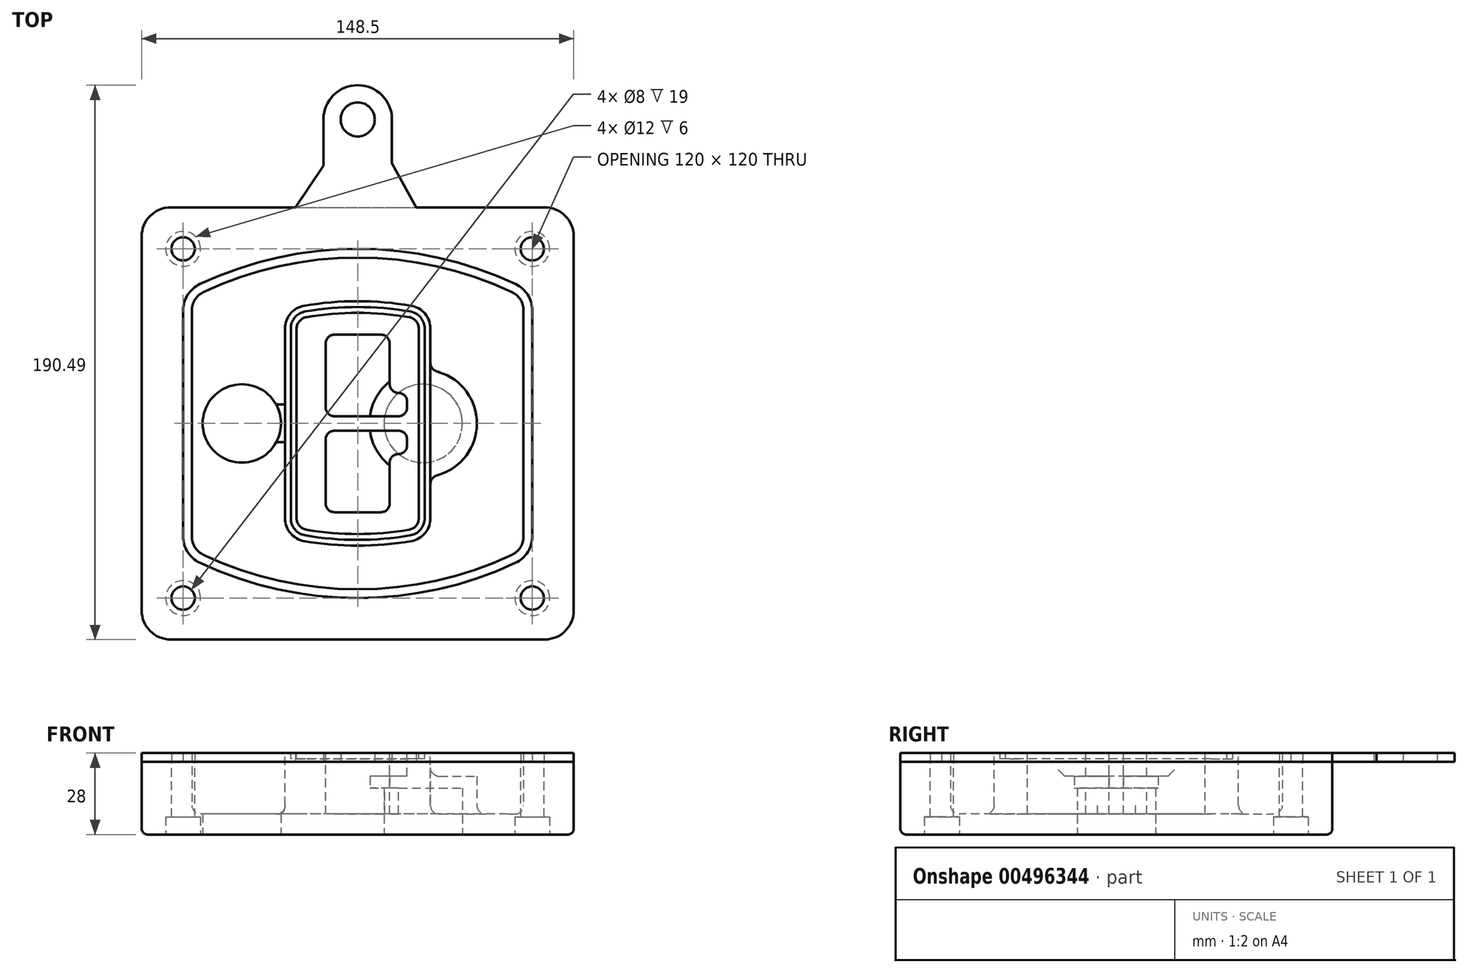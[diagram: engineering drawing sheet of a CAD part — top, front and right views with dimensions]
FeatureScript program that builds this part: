
annotation { "Feature Type Name" : "Feature", "Feature Type Description" : "" }
export const myFeature = defineFeature(function(context is Context, id is Id, definition is map)
    precondition{}
    {
        {
            var Q0;
            Q0=qCreatedBy(makeId("Top.planeOp"),FACE);
            var sketch = newSketch(context, id + "F0", { "sketchPlane" : qUnion([Q0])});
            skPoint(sketch, "E0.rect.middle", {"position": v(0, 0) * mm});
            skLineSegment(sketch, "E1.bottom", {"start": v(-64.25, -74.25) * mm, "end": v(64.25, -74.25) * mm});
            skLineSegment(sketch, "E1.top", {"start": v(-64.25, 74.25) * mm, "end": v(64.25, 74.25) * mm});
            skLineSegment(sketch, "E1.left", {"start": v(-74.25, -64.25) * mm, "end": v(-74.25, 64.25) * mm});
            skLineSegment(sketch, "E1.right", {"start": v(74.25, -64.25) * mm, "end": v(74.25, 64.25) * mm});
            skLineSegment(sketch, "E2", {"start": v(-74.25, 74.25) * mm, "end": v(74.25, -74.25) * mm, "construction": true});
            skLineSegment(sketch, "E3", {"start": v(74.25, 74.25) * mm, "end": v(-74.25, -74.25) * mm, "construction": true});
            skCircle(sketch, "E4", {"center": v(-60, 60) * mm, "radius": 4 * mm});
            skCircle(sketch, "E5", {"center": v(60, 60) * mm, "radius": 4 * mm});
            skCircle(sketch, "E6", {"center": v(60, -60) * mm, "radius": 4 * mm});
            skCircle(sketch, "E7", {"center": v(-60, -60) * mm, "radius": 4 * mm});
            skLineSegment(sketch, "E8", {"start": v(-60, 60) * mm, "end": v(60, 60) * mm, "construction": true});
            skLineSegment(sketch, "E9", {"start": v(60, 60) * mm, "end": v(60, -60) * mm, "construction": true});
            skLineSegment(sketch, "E10", {"start": v(60, -60) * mm, "end": v(-60, -60) * mm, "construction": true});
            skLineSegment(sketch, "E11", {"start": v(-60, -60) * mm, "end": v(-60, 60) * mm, "construction": true});
            skLineSegment(sketch, "E12", {"start": v(-60, 38.83) * mm, "end": v(-60, -38.83) * mm});
            skLineSegment(sketch, "E13", {"start": v(60, 38.83) * mm, "end": v(60, -38.83) * mm});
            skArc(sketch, "E14", {"start": v(54.26, 47.88) * mm, "mid": v(0, 60) * mm, "end": v(-54.26, 47.88) * mm});
            skArc(sketch, "E15", {"start": v(-54.26, -47.88) * mm, "mid": v(0, -60) * mm, "end": v(54.26, -47.88) * mm});
            skLineSegment(sketch, "E16", {"start": v(-60, 0) * mm, "end": v(60, 0) * mm, "construction": true});
            skPoint(sketch, "E17.visualSharp", {"position": v(-60, -45) * mm});
            skArc(sketch, "E17.filletArc", {"start": v(-60, -38.83) * mm, "mid": v(-58.44, -44.2) * mm, "end": v(-54.26, -47.88) * mm});
            skPoint(sketch, "E18.visualSharp", {"position": v(-60, 45) * mm});
            skArc(sketch, "E18.filletArc", {"start": v(-54.26, 47.88) * mm, "mid": v(-58.44, 44.2) * mm, "end": v(-60, 38.83) * mm});
            skPoint(sketch, "E19.visualSharp", {"position": v(60, 45) * mm});
            skArc(sketch, "E19.filletArc", {"start": v(60, 38.83) * mm, "mid": v(58.44, 44.2) * mm, "end": v(54.26, 47.88) * mm});
            skPoint(sketch, "E20.visualSharp", {"position": v(60, -45) * mm});
            skArc(sketch, "E20.filletArc", {"start": v(54.26, -47.88) * mm, "mid": v(58.44, -44.2) * mm, "end": v(60, -38.83) * mm});
            skPoint(sketch, "E21.visualSharp", {"position": v(-74.25, 74.25) * mm});
            skArc(sketch, "E21.filletArc", {"start": v(-64.25, 74.25) * mm, "mid": v(-71.32, 71.32) * mm, "end": v(-74.25, 64.25) * mm});
            skPoint(sketch, "E22.visualSharp", {"position": v(74.25, 74.25) * mm});
            skArc(sketch, "E22.filletArc", {"start": v(74.25, 64.25) * mm, "mid": v(71.32, 71.32) * mm, "end": v(64.25, 74.25) * mm});
            skPoint(sketch, "E23.visualSharp", {"position": v(74.25, -74.25) * mm});
            skArc(sketch, "E23.filletArc", {"start": v(64.25, -74.25) * mm, "mid": v(71.32, -71.32) * mm, "end": v(74.25, -64.25) * mm});
            skPoint(sketch, "E24.visualSharp", {"position": v(-74.25, -74.25) * mm});
            skArc(sketch, "E24.filletArc", {"start": v(-74.25, -64.25) * mm, "mid": v(-71.32, -71.32) * mm, "end": v(-64.25, -74.25) * mm});
            skArc(sketch, "E25.0", {"start": v(57, 38.83) * mm, "mid": v(55.9, 42.58) * mm, "end": v(52.98, 45.17) * mm});
            skLineSegment(sketch, "E25.1", {"start": v(57, 38.83) * mm, "end": v(57, -38.83) * mm});
            skArc(sketch, "E25.2", {"start": v(52.98, -45.17) * mm, "mid": v(55.9, -42.58) * mm, "end": v(57, -38.83) * mm});
            skArc(sketch, "E25.3", {"start": v(-52.98, -45.17) * mm, "mid": v(0, -57) * mm, "end": v(52.98, -45.17) * mm});
            skArc(sketch, "E25.4", {"start": v(-57, -38.83) * mm, "mid": v(-55.9, -42.58) * mm, "end": v(-52.98, -45.17) * mm});
            skArc(sketch, "E25.5", {"start": v(52.98, 45.17) * mm, "mid": v(0, 57) * mm, "end": v(-52.98, 45.17) * mm});
            skLineSegment(sketch, "E25.6", {"start": v(-57, 38.83) * mm, "end": v(-57, -38.83) * mm});
            skArc(sketch, "E25.7", {"start": v(-52.98, 45.17) * mm, "mid": v(-55.9, 42.58) * mm, "end": v(-57, 38.83) * mm});
            skArc(sketch, "E26.0", {"start": v(-55.96, 51.5) * mm, "mid": v(-61.82, 46.33) * mm, "end": v(-64, 38.83) * mm});
            skArc(sketch, "E26.1", {"start": v(55.96, 51.5) * mm, "mid": v(0, 64) * mm, "end": v(-55.96, 51.5) * mm});
            skArc(sketch, "E26.2", {"start": v(64, 38.83) * mm, "mid": v(61.82, 46.33) * mm, "end": v(55.96, 51.5) * mm});
            skLineSegment(sketch, "E26.3", {"start": v(64, 38.83) * mm, "end": v(64, -38.83) * mm});
            skArc(sketch, "E26.4", {"start": v(55.96, -51.5) * mm, "mid": v(61.82, -46.33) * mm, "end": v(64, -38.83) * mm});
            skLineSegment(sketch, "E26.5", {"start": v(-64, 38.83) * mm, "end": v(-64, -38.83) * mm});
            skArc(sketch, "E26.6", {"start": v(-55.96, -51.5) * mm, "mid": v(0, -64) * mm, "end": v(55.96, -51.5) * mm});
            skArc(sketch, "E26.7", {"start": v(-64, -38.83) * mm, "mid": v(-61.82, -46.33) * mm, "end": v(-55.96, -51.5) * mm});
            skSolve(sketch);
        }
        {
            var Q0;
            Q0=makeQuery(id+"F0.imprint","IMPRINT",FACE,{"disambiguationData":[TD([[makeQuery(id+"F0.imprint","IMPRINT",EDGE,{"derivedFrom":sQuery(id+"F0.wireOp",EDGE,"E1.bottom")}),1.0]])]});
            var Q1;
            Q1=makeQuery(id+"F0.imprint","IMPRINT",FACE,{"disambiguationData":[TD([[makeQuery(id+"F0.imprint","IMPRINT",EDGE,{"derivedFrom":sQuery(id+"F0.wireOp",EDGE,"E12")}),1.0]])]});
            var Q2;
            Q2=makeQuery(id+"F0.imprint","IMPRINT",FACE,{"disambiguationData":[TD([[makeQuery(id+"F0.imprint","IMPRINT",EDGE,{"derivedFrom":sQuery(id+"F0.wireOp",EDGE,"E25.0")}),1.0]])]});
            var Q3;
            Q3=makeQuery(id+"F0.imprint","IMPRINT",FACE,{"disambiguationData":[TD([[makeQuery(id+"F0.imprint","IMPRINT",EDGE,{"derivedFrom":sQuery(id+"F0.wireOp",EDGE,"E12")}),-1.0]])]});
            extrude(context, id + "F1", {"entities" : qUnion([Q0, Q1, Q2, Q3]), "oppositeDirection" : true, "depth" : 25 * mm});
        }
        {
            var Q0;
            Q0=makeQuery(id+"F0.imprint","IMPRINT",FACE,{"disambiguationData":[TD([[makeQuery(id+"F0.imprint","IMPRINT",EDGE,{"derivedFrom":sQuery(id+"F0.wireOp",EDGE,"E12")}),1.0]])]});
            extrude(context, id + "F2", {"entities" : qUnion([Q0]), "operationType" : NewBodyOperationType.ADD, "depth" : 3 * mm});
        }
        {
            var Q0;
            Q0=makeQuery(id+"F0.imprint","IMPRINT",FACE,{"disambiguationData":[TD([[makeQuery(id+"F0.imprint","IMPRINT",EDGE,{"derivedFrom":sQuery(id+"F0.wireOp",EDGE,"E25.0")}),1.0]])]});
            extrude(context, id + "F3", {"entities" : qUnion([Q0]), "operationType" : NewBodyOperationType.REMOVE, "oppositeDirection" : true, "depth" : 18 * mm});
        }
        {
            var Q0;
            Q0=makeQuery(id+"F2.opExtrude","CAP_FACE",FACE,{"disambiguationData":[OSD([sQuery(id+"F0.wireOp",EDGE,"E12"),sQuery(id+"F0.wireOp",EDGE,"E13"),sQuery(id+"F0.wireOp",EDGE,"E14"),sQuery(id+"F0.wireOp",EDGE,"E15"),sQuery(id+"F0.wireOp",EDGE,"E17.filletArc"),sQuery(id+"F0.wireOp",EDGE,"E18.filletArc"),sQuery(id+"F0.wireOp",EDGE,"E19.filletArc"),sQuery(id+"F0.wireOp",EDGE,"E20.filletArc"),sQuery(id+"F0.wireOp",EDGE,"E25.0"),sQuery(id+"F0.wireOp",EDGE,"E25.1"),sQuery(id+"F0.wireOp",EDGE,"E25.2"),sQuery(id+"F0.wireOp",EDGE,"E25.3"),sQuery(id+"F0.wireOp",EDGE,"E25.4"),sQuery(id+"F0.wireOp",EDGE,"E25.5"),sQuery(id+"F0.wireOp",EDGE,"E25.6"),sQuery(id+"F0.wireOp",EDGE,"E25.7")])],"isStart":false});
            var sketch = newSketch(context, id + "F4", { "sketchPlane" : qUnion([Q0])});
            skArc(sketch, "E27.0", {"start": v(-18.34, -40.45) * mm, "mid": v(0, -42) * mm, "end": v(18.34, -40.45) * mm});
            skArc(sketch, "E28.0", {"start": v(18.34, 40.45) * mm, "mid": v(0, 42) * mm, "end": v(-18.34, 40.45) * mm});
            skLineSegment(sketch, "E29", {"start": v(-25, 32.57) * mm, "end": v(-25, -32.57) * mm});
            skLineSegment(sketch, "E30", {"start": v(25, 32.57) * mm, "end": v(25, -32.57) * mm});
            skLineSegment(sketch, "E31", {"start": v(-25, 39.1) * mm, "end": v(25, 39.1) * mm, "construction": true});
            skLineSegment(sketch, "E32", {"start": v(-25, -39.1) * mm, "end": v(25, -39.1) * mm, "construction": true});
            skPoint(sketch, "E33.visualSharp", {"position": v(-25, 39.1) * mm});
            skArc(sketch, "E33.filletArc", {"start": v(-18.34, 40.45) * mm, "mid": v(-23.11, 37.73) * mm, "end": v(-25, 32.57) * mm});
            skPoint(sketch, "E34.visualSharp", {"position": v(25, 39.1) * mm});
            skArc(sketch, "E34.filletArc", {"start": v(25, 32.57) * mm, "mid": v(23.11, 37.73) * mm, "end": v(18.34, 40.45) * mm});
            skPoint(sketch, "E35.visualSharp", {"position": v(25, -39.1) * mm});
            skArc(sketch, "E35.filletArc", {"start": v(18.34, -40.45) * mm, "mid": v(23.11, -37.73) * mm, "end": v(25, -32.57) * mm});
            skPoint(sketch, "E36.visualSharp", {"position": v(-25, -39.1) * mm});
            skArc(sketch, "E36.filletArc", {"start": v(-25, -32.57) * mm, "mid": v(-23.11, -37.73) * mm, "end": v(-18.34, -40.45) * mm});
            skArc(sketch, "E37.0", {"start": v(52.98, 45.17) * mm, "mid": v(0, 57) * mm, "end": v(-52.98, 45.17) * mm});
            skArc(sketch, "E37.1", {"start": v(-52.98, 45.17) * mm, "mid": v(-55.9, 42.58) * mm, "end": v(-57, 38.83) * mm});
            skLineSegment(sketch, "E37.2", {"start": v(-57, 38.83) * mm, "end": v(-57, -38.83) * mm});
            skArc(sketch, "E37.3", {"start": v(-57, -38.83) * mm, "mid": v(-55.9, -42.58) * mm, "end": v(-52.98, -45.17) * mm});
            skArc(sketch, "E37.4", {"start": v(-52.98, -45.17) * mm, "mid": v(0, -57) * mm, "end": v(52.98, -45.17) * mm});
            skArc(sketch, "E37.5", {"start": v(52.98, -45.17) * mm, "mid": v(55.9, -42.58) * mm, "end": v(57, -38.83) * mm});
            skLineSegment(sketch, "E37.6", {"start": v(57, 38.83) * mm, "end": v(57, -38.83) * mm});
            skArc(sketch, "E37.7", {"start": v(57, 38.83) * mm, "mid": v(55.9, 42.58) * mm, "end": v(52.98, 45.17) * mm});
            skLineSegment(sketch, "E38.0", {"start": v(23, 32.57) * mm, "end": v(23, -32.57) * mm});
            skArc(sketch, "E38.1", {"start": v(18, -38.48) * mm, "mid": v(21.58, -36.44) * mm, "end": v(23, -32.57) * mm});
            skArc(sketch, "E38.2", {"start": v(-18, -38.48) * mm, "mid": v(0, -40) * mm, "end": v(18, -38.48) * mm});
            skArc(sketch, "E38.3", {"start": v(-23, -32.57) * mm, "mid": v(-21.58, -36.44) * mm, "end": v(-18, -38.48) * mm});
            skLineSegment(sketch, "E38.4", {"start": v(-23, 32.57) * mm, "end": v(-23, -32.57) * mm});
            skArc(sketch, "E38.5", {"start": v(23, 32.57) * mm, "mid": v(21.58, 36.44) * mm, "end": v(18, 38.48) * mm});
            skArc(sketch, "E38.6", {"start": v(-18, 38.48) * mm, "mid": v(-21.58, 36.44) * mm, "end": v(-23, 32.57) * mm});
            skArc(sketch, "E38.7", {"start": v(18, 38.48) * mm, "mid": v(0, 40) * mm, "end": v(-18, 38.48) * mm});
            skArc(sketch, "E39.0", {"start": v(21, 32.57) * mm, "mid": v(20.06, 35.15) * mm, "end": v(17.67, 36.5) * mm});
            skLineSegment(sketch, "E39.1", {"start": v(21, 32.57) * mm, "end": v(21, -32.57) * mm});
            skArc(sketch, "E39.2", {"start": v(17.67, -36.5) * mm, "mid": v(20.06, -35.15) * mm, "end": v(21, -32.57) * mm});
            skArc(sketch, "E39.3", {"start": v(-17.67, -36.5) * mm, "mid": v(0, -38) * mm, "end": v(17.67, -36.5) * mm});
            skArc(sketch, "E39.4", {"start": v(-21, -32.57) * mm, "mid": v(-20.06, -35.15) * mm, "end": v(-17.67, -36.5) * mm});
            skArc(sketch, "E39.5", {"start": v(17.67, 36.5) * mm, "mid": v(0, 38) * mm, "end": v(-17.67, 36.5) * mm});
            skLineSegment(sketch, "E39.6", {"start": v(-21, 32.57) * mm, "end": v(-21, -32.57) * mm});
            skArc(sketch, "E39.7", {"start": v(-17.67, 36.5) * mm, "mid": v(-20.06, 35.15) * mm, "end": v(-21, 32.57) * mm});
            skLineSegment(sketch, "E40", {"start": v(-25, 0) * mm, "end": v(25, 0) * mm, "construction": true});
            skLineSegment(sketch, "E41", {"start": v(-11, 5.5) * mm, "end": v(-11, 27.5) * mm});
            skLineSegment(sketch, "E42", {"start": v(-8, 30.5) * mm, "end": v(8, 30.5) * mm});
            skLineSegment(sketch, "E43", {"start": v(11, 27.5) * mm, "end": v(11, 13.5) * mm});
            skLineSegment(sketch, "E44", {"start": v(14, 10.5) * mm, "end": v(14, 10.5) * mm});
            skLineSegment(sketch, "E45", {"start": v(17, 7.5) * mm, "end": v(17, 5.5) * mm});
            skLineSegment(sketch, "E46", {"start": v(14, 2.5) * mm, "end": v(-8, 2.5) * mm});
            skPoint(sketch, "E47.visualSharp", {"position": v(-11, 30.5) * mm});
            skArc(sketch, "E47.filletArc", {"start": v(-8, 30.5) * mm, "mid": v(-10.12, 29.62) * mm, "end": v(-11, 27.5) * mm});
            skPoint(sketch, "E48.visualSharp", {"position": v(11, 30.5) * mm});
            skArc(sketch, "E48.filletArc", {"start": v(11, 27.5) * mm, "mid": v(10.12, 29.62) * mm, "end": v(8, 30.5) * mm});
            skPoint(sketch, "E49.visualSharp", {"position": v(11, 10.5) * mm});
            skArc(sketch, "E49.filletArc", {"start": v(11, 13.5) * mm, "mid": v(11.88, 11.38) * mm, "end": v(14, 10.5) * mm});
            skPoint(sketch, "E50.visualSharp", {"position": v(17, 10.5) * mm});
            skArc(sketch, "E50.filletArc", {"start": v(17, 7.5) * mm, "mid": v(16.12, 9.62) * mm, "end": v(14, 10.5) * mm});
            skPoint(sketch, "E51.visualSharp", {"position": v(17, 2.5) * mm});
            skArc(sketch, "E51.filletArc", {"start": v(14, 2.5) * mm, "mid": v(16.12, 3.38) * mm, "end": v(17, 5.5) * mm});
            skPoint(sketch, "E52.visualSharp", {"position": v(-11, 2.5) * mm});
            skArc(sketch, "E52.filletArc", {"start": v(-11, 5.5) * mm, "mid": v(-10.12, 3.38) * mm, "end": v(-8, 2.5) * mm});
            skLineSegment(sketch, "E53.0.MirrorCS", {"start": v(14, -2.5) * mm, "end": v(-8, -2.5) * mm});
            skArc(sketch, "E54.0.MirrorCS", {"start": v(-11, -5.5) * mm, "mid": v(-10.12, -3.38) * mm, "end": v(-8, -2.5) * mm});
            skLineSegment(sketch, "E55.0.MirrorCS", {"start": v(-11, -5.5) * mm, "end": v(-11, -27.5) * mm});
            skArc(sketch, "E56.0.MirrorCS", {"start": v(-8, -30.5) * mm, "mid": v(-10.12, -29.62) * mm, "end": v(-11, -27.5) * mm});
            skLineSegment(sketch, "E57.0.MirrorCS", {"start": v(-8, -30.5) * mm, "end": v(8, -30.5) * mm});
            skArc(sketch, "E58.0.MirrorCS", {"start": v(11, -27.5) * mm, "mid": v(10.12, -29.62) * mm, "end": v(8, -30.5) * mm});
            skLineSegment(sketch, "E59.0.MirrorCS", {"start": v(11, -27.5) * mm, "end": v(11, -13.5) * mm});
            skArc(sketch, "E60.0.MirrorCS", {"start": v(11, -13.5) * mm, "mid": v(11.88, -11.38) * mm, "end": v(14, -10.5) * mm});
            skArc(sketch, "E61.0.MirrorCS", {"start": v(17, -7.5) * mm, "mid": v(16.12, -9.62) * mm, "end": v(14, -10.5) * mm});
            skLineSegment(sketch, "E62.0.MirrorCS", {"start": v(17, -7.5) * mm, "end": v(17, -5.5) * mm});
            skArc(sketch, "E63.0.MirrorCS", {"start": v(14, -2.5) * mm, "mid": v(16.12, -3.38) * mm, "end": v(17, -5.5) * mm});
            skSolve(sketch);
        }
        {
            var Q0;
            Q0=makeQuery(id+"F4.imprint","IMPRINT",FACE,{"disambiguationData":[TD([[makeQuery(id+"F4.imprint","IMPRINT",EDGE,{"derivedFrom":sQuery(id+"F4.wireOp",EDGE,"E27.0")}),1.0]])]});
            var Q1;
            Q1=makeQuery(id+"F4.imprint","IMPRINT",FACE,{"disambiguationData":[TD([[makeQuery(id+"F4.imprint","IMPRINT",EDGE,{"derivedFrom":sQuery(id+"F4.wireOp",EDGE,"E38.0")}),-1.0]])]});
            var Q2;
            Q2=makeQuery(id+"F4.imprint","IMPRINT",FACE,{"disambiguationData":[TD([[makeQuery(id+"F4.imprint","IMPRINT",EDGE,{"derivedFrom":sQuery(id+"F4.wireOp",EDGE,"E39.0")}),1.0]])]});
            extrude(context, id + "F5", {"entities" : qUnion([Q0, Q1, Q2]), "operationType" : NewBodyOperationType.ADD, "endBound" : BoundingType.UP_TO_NEXT, "oppositeDirection" : true, "depth" : 25 * mm});
        }
        {
            var Q0;
            Q0=makeQuery(id+"F4.imprint","IMPRINT",FACE,{"disambiguationData":[TD([[makeQuery(id+"F4.imprint","IMPRINT",EDGE,{"derivedFrom":sQuery(id+"F4.wireOp",EDGE,"E38.0")}),-1.0]])]});
            extrude(context, id + "F6", {"entities" : qUnion([Q0]), "operationType" : NewBodyOperationType.REMOVE, "oppositeDirection" : true, "depth" : 2 * mm});
        }
        {
            var Q0;
            Q0=makeQuery(id+"F1.opExtrude","CAP_FACE",FACE,{"disambiguationData":[OSD([sQuery(id+"F0.wireOp",EDGE,"E1.bottom"),sQuery(id+"F0.wireOp",EDGE,"E1.top"),sQuery(id+"F0.wireOp",EDGE,"E1.left"),sQuery(id+"F0.wireOp",EDGE,"E1.right"),sQuery(id+"F0.wireOp",EDGE,"E4"),sQuery(id+"F0.wireOp",EDGE,"E5"),sQuery(id+"F0.wireOp",EDGE,"E6"),sQuery(id+"F0.wireOp",EDGE,"E7"),sQuery(id+"F0.wireOp",EDGE,"E21.filletArc"),sQuery(id+"F0.wireOp",EDGE,"E22.filletArc"),sQuery(id+"F0.wireOp",EDGE,"E23.filletArc"),sQuery(id+"F0.wireOp",EDGE,"E24.filletArc")])],"isStart":false});
            var sketch = newSketch(context, id + "F7", { "sketchPlane" : qUnion([Q0])});
            skCircle(sketch, "E64", {"center": v(22.5, 0) * mm, "radius": 13.47 * mm});
            skCircle(sketch, "E65", {"center": v(-39.81, 0) * mm, "radius": 13.47 * mm});
            skLineSegment(sketch, "E66", {"start": v(74.25, 0) * mm, "end": v(-74.25, 0) * mm});
            skCircle(sketch, "E67", {"center": v(22.5, 0) * mm, "radius": 18.47 * mm});
            skCircle(sketch, "E68", {"center": v(60, -60) * mm, "radius": 6 * mm});
            skCircle(sketch, "E69", {"center": v(-60, -60) * mm, "radius": 6 * mm});
            skCircle(sketch, "E70", {"center": v(-60, 60) * mm, "radius": 6 * mm});
            skCircle(sketch, "E71", {"center": v(60, 60) * mm, "radius": 6 * mm});
            skSolve(sketch);
        }
        {
            var Q0;
            {var subQ1=sQuery(id+"F7.wireOp",EDGE,"E66");var subQ4=sQuery(id+"F7.wireOp",EDGE,"E64");var subQ6=makeQuery(id+"F7.imprint","INTERSECT",VERTEX,{"disambiguationData":[OD(0.0)],"derivedFrom":[subQ4,subQ1]});Q0=makeQuery(id+"F7.imprint","IMPRINT",FACE,{"disambiguationData":[TD([[makeQuery(id+"F7.imprint","IMPRINT",EDGE,{"disambiguationData":[TD([[subQ6,-1.0]])],"derivedFrom":subQ4}),-1.0]])]});}
            var Q1;
            {var subQ0=sQuery(id+"F7.wireOp",EDGE,"E66");var subQ1=sQuery(id+"F7.wireOp",EDGE,"E64");var subQ3=makeQuery(id+"F7.imprint","INTERSECT",VERTEX,{"disambiguationData":[OD(0.0)],"derivedFrom":[subQ1,subQ0]});Q1=makeQuery(id+"F7.imprint","IMPRINT",FACE,{"disambiguationData":[TD([[makeQuery(id+"F7.imprint","IMPRINT",EDGE,{"disambiguationData":[TD([[subQ3,-1.0]])],"derivedFrom":subQ1}),1.0]])]});}
            var Q2;
            {var subQ0=sQuery(id+"F7.wireOp",EDGE,"E66");var subQ1=sQuery(id+"F7.wireOp",EDGE,"E64");var subQ3=makeQuery(id+"F7.imprint","INTERSECT",VERTEX,{"disambiguationData":[OD(0.0)],"derivedFrom":[subQ1,subQ0]});Q2=makeQuery(id+"F7.imprint","IMPRINT",FACE,{"disambiguationData":[TD([[makeQuery(id+"F7.imprint","IMPRINT",EDGE,{"disambiguationData":[TD([[subQ3,1.0]])],"derivedFrom":subQ1}),1.0]])]});}
            var Q3;
            {var subQ1=sQuery(id+"F7.wireOp",EDGE,"E66");var subQ4=sQuery(id+"F7.wireOp",EDGE,"E64");var subQ6=makeQuery(id+"F7.imprint","INTERSECT",VERTEX,{"disambiguationData":[OD(0.0)],"derivedFrom":[subQ4,subQ1]});Q3=makeQuery(id+"F7.imprint","IMPRINT",FACE,{"disambiguationData":[TD([[makeQuery(id+"F7.imprint","IMPRINT",EDGE,{"disambiguationData":[TD([[subQ6,1.0]])],"derivedFrom":subQ4}),-1.0]])]});}
            extrude(context, id + "F8", {"entities" : qUnion([Q0, Q1, Q2, Q3]), "operationType" : NewBodyOperationType.ADD, "oppositeDirection" : true, "depth" : 20 * mm});
        }
        {
            var Q0;
            {var subQ0=sQuery(id+"F7.wireOp",EDGE,"E66");var subQ1=sQuery(id+"F7.wireOp",EDGE,"E64");var subQ3=makeQuery(id+"F7.imprint","INTERSECT",VERTEX,{"disambiguationData":[OD(0.0)],"derivedFrom":[subQ1,subQ0]});Q0=makeQuery(id+"F7.imprint","IMPRINT",FACE,{"disambiguationData":[TD([[makeQuery(id+"F7.imprint","IMPRINT",EDGE,{"disambiguationData":[TD([[subQ3,-1.0]])],"derivedFrom":subQ1}),1.0]])]});}
            var Q1;
            {var subQ0=sQuery(id+"F7.wireOp",EDGE,"E66");var subQ1=sQuery(id+"F7.wireOp",EDGE,"E64");var subQ3=makeQuery(id+"F7.imprint","INTERSECT",VERTEX,{"disambiguationData":[OD(0.0)],"derivedFrom":[subQ1,subQ0]});Q1=makeQuery(id+"F7.imprint","IMPRINT",FACE,{"disambiguationData":[TD([[makeQuery(id+"F7.imprint","IMPRINT",EDGE,{"disambiguationData":[TD([[subQ3,1.0]])],"derivedFrom":subQ1}),1.0]])]});}
            extrude(context, id + "F9", {"entities" : qUnion([Q0, Q1]), "operationType" : NewBodyOperationType.REMOVE, "oppositeDirection" : true, "depth" : 16 * mm});
        }
        {
            var Q0;
            {var subQ0=sQuery(id+"F7.wireOp",EDGE,"E66");var subQ1=sQuery(id+"F7.wireOp",EDGE,"E65");var subQ3=makeQuery(id+"F7.imprint","INTERSECT",VERTEX,{"disambiguationData":[OD(0.0)],"derivedFrom":[subQ1,subQ0]});Q0=makeQuery(id+"F7.imprint","IMPRINT",FACE,{"disambiguationData":[TD([[makeQuery(id+"F7.imprint","IMPRINT",EDGE,{"disambiguationData":[TD([[subQ3,-1.0]])],"derivedFrom":subQ1}),1.0]])]});}
            var Q1;
            {var subQ0=sQuery(id+"F7.wireOp",EDGE,"E66");var subQ1=sQuery(id+"F7.wireOp",EDGE,"E65");var subQ3=makeQuery(id+"F7.imprint","INTERSECT",VERTEX,{"disambiguationData":[OD(0.0)],"derivedFrom":[subQ1,subQ0]});Q1=makeQuery(id+"F7.imprint","IMPRINT",FACE,{"disambiguationData":[TD([[makeQuery(id+"F7.imprint","IMPRINT",EDGE,{"disambiguationData":[TD([[subQ3,1.0]])],"derivedFrom":subQ1}),1.0]])]});}
            extrude(context, id + "F10", {"entities" : qUnion([Q0, Q1]), "operationType" : NewBodyOperationType.REMOVE, "oppositeDirection" : true, "depth" : 25 * mm});
        }
        {
            var Q0;
            Q0=makeQuery(id+"F7.imprint","IMPRINT",FACE,{"disambiguationData":[TD([[makeQuery(id+"F7.imprint","IMPRINT",EDGE,{"derivedFrom":sQuery(id+"F7.wireOp",EDGE,"E68")}),1.0]])]});
            var Q1;
            Q1=makeQuery(id+"F7.imprint","IMPRINT",FACE,{"disambiguationData":[TD([[makeQuery(id+"F7.imprint","IMPRINT",EDGE,{"derivedFrom":makeQuery(id+"F1.opExtrude","CAP_EDGE",EDGE,{"disambiguationData":[OSD([sQuery(id+"F0.wireOp",EDGE,"E5")])],"isStart":false})}),-1.0]])]});
            var Q2;
            Q2=makeQuery(id+"F7.imprint","IMPRINT",FACE,{"disambiguationData":[TD([[makeQuery(id+"F7.imprint","IMPRINT",EDGE,{"derivedFrom":sQuery(id+"F7.wireOp",EDGE,"E69")}),1.0]])]});
            var Q3;
            Q3=makeQuery(id+"F7.imprint","IMPRINT",FACE,{"disambiguationData":[TD([[makeQuery(id+"F7.imprint","IMPRINT",EDGE,{"derivedFrom":makeQuery(id+"F1.opExtrude","CAP_EDGE",EDGE,{"disambiguationData":[OSD([sQuery(id+"F0.wireOp",EDGE,"E4")])],"isStart":false})}),-1.0]])]});
            var Q4;
            Q4=makeQuery(id+"F7.imprint","IMPRINT",FACE,{"disambiguationData":[TD([[makeQuery(id+"F7.imprint","IMPRINT",EDGE,{"derivedFrom":sQuery(id+"F7.wireOp",EDGE,"E70")}),1.0]])]});
            var Q5;
            Q5=makeQuery(id+"F7.imprint","IMPRINT",FACE,{"disambiguationData":[TD([[makeQuery(id+"F7.imprint","IMPRINT",EDGE,{"derivedFrom":makeQuery(id+"F1.opExtrude","CAP_EDGE",EDGE,{"disambiguationData":[OSD([sQuery(id+"F0.wireOp",EDGE,"E7")])],"isStart":false})}),-1.0]])]});
            var Q6;
            Q6=makeQuery(id+"F7.imprint","IMPRINT",FACE,{"disambiguationData":[TD([[makeQuery(id+"F7.imprint","IMPRINT",EDGE,{"derivedFrom":sQuery(id+"F7.wireOp",EDGE,"E71")}),1.0]])]});
            var Q7;
            Q7=makeQuery(id+"F7.imprint","IMPRINT",FACE,{"disambiguationData":[TD([[makeQuery(id+"F7.imprint","IMPRINT",EDGE,{"derivedFrom":makeQuery(id+"F1.opExtrude","CAP_EDGE",EDGE,{"disambiguationData":[OSD([sQuery(id+"F0.wireOp",EDGE,"E6")])],"isStart":false})}),-1.0]])]});
            extrude(context, id + "F11", {"entities" : qUnion([Q0, Q1, Q2, Q3, Q4, Q5, Q6, Q7]), "operationType" : NewBodyOperationType.REMOVE, "oppositeDirection" : true, "depth" : 6 * mm});
        }
        {
            var Q0;
            Q0=makeQuery(id+"F9.boolean.opBoolean","COPY",FACE,{"derivedFrom":makeQuery(id+"F9.opExtrude","CAP_FACE",FACE,{"disambiguationData":[OSD([sQuery(id+"F7.wireOp",EDGE,"E64")])],"isStart":false})});
            var sketch = newSketch(context, id + "F12", { "sketchPlane" : qUnion([Q0])});
            skArc(sketch, "E72.0", {"start": v(11, 14.45) * mm, "mid": v(6.45, 9.13) * mm, "end": v(4.2, 2.5) * mm});
            skArc(sketch, "E72.1", {"start": v(4.2, -2.5) * mm, "mid": v(6.45, -9.13) * mm, "end": v(11, -14.45) * mm});
            skLineSegment(sketch, "E73", {"start": v(4.2, -2.5) * mm, "end": v(14, -2.5) * mm});
            skLineSegment(sketch, "E74.0", {"start": v(14, 2.5) * mm, "end": v(4.2, 2.5) * mm});
            skArc(sketch, "E74.1", {"start": v(14, 2.5) * mm, "mid": v(16.12, 3.38) * mm, "end": v(17, 5.5) * mm});
            skLineSegment(sketch, "E74.2", {"start": v(17, 7.5) * mm, "end": v(17, 5.5) * mm});
            skArc(sketch, "E74.3", {"start": v(17, 7.5) * mm, "mid": v(16.12, 9.62) * mm, "end": v(14, 10.5) * mm});
            skArc(sketch, "E74.4", {"start": v(11, 13.5) * mm, "mid": v(11.88, 11.38) * mm, "end": v(14, 10.5) * mm});
            skLineSegment(sketch, "E74.5", {"start": v(11, 14.45) * mm, "end": v(11, 13.5) * mm});
            skLineSegment(sketch, "E74.7", {"start": v(14, -2.5) * mm, "end": v(4.2, -2.5) * mm});
            skArc(sketch, "E74.8", {"start": v(14, -2.5) * mm, "mid": v(16.12, -3.38) * mm, "end": v(17, -5.5) * mm});
            skLineSegment(sketch, "E74.9", {"start": v(17, -7.5) * mm, "end": v(17, -5.5) * mm});
            skArc(sketch, "E74.10", {"start": v(17, -7.5) * mm, "mid": v(16.12, -9.62) * mm, "end": v(14, -10.5) * mm});
            skArc(sketch, "E74.11", {"start": v(11, -13.5) * mm, "mid": v(11.88, -11.38) * mm, "end": v(14, -10.5) * mm});
            skLineSegment(sketch, "E74.12", {"start": v(11, -14.45) * mm, "end": v(11, -13.5) * mm});
            skPoint(sketch, "E75.orphan", {"position": v(11, -27.5) * mm});
            skPoint(sketch, "E76.orphan", {"position": v(-8, -2.5) * mm});
            skPoint(sketch, "E77.orphan", {"position": v(-8, 2.5) * mm});
            skPoint(sketch, "E78.orphan", {"position": v(11, 27.5) * mm});
            skSolve(sketch);
        }
        {
            var Q0;
            {var subQ7=sQuery(id+"F12.wireOp",EDGE,"E72.0");var subQ14=sQuery(id+"F12.wireOp",EDGE,"E72.1");var subQ16=sQuery(id+"F12.wireOp",EDGE,"E74.1");var subQ18=sQuery(id+"F12.wireOp",EDGE,"E74.8");Q0=qUnion([makeQuery(id+"F12.imprint","IMPRINT",FACE,{"disambiguationData":[TD([[makeQuery(id+"F12.imprint","IMPRINT",EDGE,{"derivedFrom":subQ7}),1.0]])]}),makeQuery(id+"F12.imprint","IMPRINT",FACE,{"disambiguationData":[TD([[makeQuery(id+"F12.imprint","IMPRINT",EDGE,{"derivedFrom":subQ14}),1.0]])]}),makeQuery(id+"F12.imprint","IMPRINT",FACE,{"disambiguationData":[TD([[makeQuery(id+"F12.imprint","IMPRINT",EDGE,{"derivedFrom":subQ16}),1.0]])]}),makeQuery(id+"F12.imprint","IMPRINT",FACE,{"disambiguationData":[TD([[makeQuery(id+"F12.imprint","IMPRINT",EDGE,{"derivedFrom":subQ18}),-1.0]])]})]);}
            var Q1;
            Q1=makeQuery(id+"F5.boolean.opBoolean","SPLIT",FACE,{"disambiguationData":[TD([makeQuery(id+"F5.opExtrude","SWEPT_FACE",FACE,{"disambiguationData":[OSD([sQuery(id+"F4.wireOp",EDGE,"E41")])]})])],"derivedFrom":makeQuery(id+"F3.boolean.opBoolean","COPY",FACE,{"derivedFrom":makeQuery(id+"F3.opExtrude","CAP_FACE",FACE,{"disambiguationData":[OSD([sQuery(id+"F0.wireOp",EDGE,"E25.0"),sQuery(id+"F0.wireOp",EDGE,"E25.1"),sQuery(id+"F0.wireOp",EDGE,"E25.2"),sQuery(id+"F0.wireOp",EDGE,"E25.3"),sQuery(id+"F0.wireOp",EDGE,"E25.4"),sQuery(id+"F0.wireOp",EDGE,"E25.5"),sQuery(id+"F0.wireOp",EDGE,"E25.6"),sQuery(id+"F0.wireOp",EDGE,"E25.7")])],"isStart":false})})});
            extrude(context, id + "F13", {"entities" : qUnion([Q0]), "operationType" : NewBodyOperationType.REMOVE, "endBound" : BoundingType.UP_TO_SURFACE, "endBoundEntityFace" : qUnion([Q1]), "depth" : 25 * mm});
        }
        {
            var Q0;
            Q0=makeQuery(id+"F3.boolean.opBoolean","COPY",EDGE,{"derivedFrom":makeQuery(id+"F3.opExtrude","CAP_EDGE",EDGE,{"disambiguationData":[OSD([sQuery(id+"F0.wireOp",EDGE,"E25.6")])],"isStart":false})});
            var Q1;
            Q1=makeQuery(id+"F8.boolean.opBoolean","INTERSECT",EDGE,{"derivedFrom":[makeQuery(id+"F5.opExtrude","SWEPT_FACE",FACE,{"disambiguationData":[OSD([sQuery(id+"F4.wireOp",EDGE,"E30")])]}),makeQuery(id+"F8.opExtrude","CAP_FACE",FACE,{"disambiguationData":[OSD([sQuery(id+"F7.wireOp",EDGE,"E67")])],"isStart":false})]});
            var Q2;
            Q2=makeQuery(id+"F8.boolean.opBoolean","INTERSECT",EDGE,{"disambiguationData":[OD(1.0)],"derivedFrom":[makeQuery(id+"F5.opExtrude","SWEPT_FACE",FACE,{"disambiguationData":[OSD([sQuery(id+"F4.wireOp",EDGE,"E30")])]}),makeQuery(id+"F8.opExtrude","SWEPT_FACE",FACE,{"disambiguationData":[OSD([sQuery(id+"F7.wireOp",EDGE,"E67")])]})]});
            var Q3;
            {var subQ0=sQuery(id+"F4.wireOp",EDGE,"E30");Q3=makeQuery(id+"F8.boolean.opBoolean","SPLIT",EDGE,{"disambiguationData":[TD([makeQuery(id+"F5.opExtrude","SWEPT_FACE",FACE,{"disambiguationData":[OSD([sQuery(id+"F4.wireOp",EDGE,"E35.filletArc")])]})])],"derivedFrom":makeQuery(id+"F5.opExtrude","CAP_EDGE",EDGE,{"disambiguationData":[OSD([subQ0])],"isStart":false})});}
            var Q4;
            {var subQ0=sQuery(id+"F0.wireOp",EDGE,"E25.7");var subQ1=sQuery(id+"F0.wireOp",EDGE,"E25.1");var subQ2=sQuery(id+"F0.wireOp",EDGE,"E25.6");var subQ3=sQuery(id+"F0.wireOp",EDGE,"E25.5");var subQ4=sQuery(id+"F0.wireOp",EDGE,"E25.4");var subQ5=sQuery(id+"F0.wireOp",EDGE,"E25.0");var subQ6=sQuery(id+"F0.wireOp",EDGE,"E25.2");var subQ7=sQuery(id+"F0.wireOp",EDGE,"E25.3");Q4=makeQuery(id+"F8.boolean.opBoolean","INTERSECT",EDGE,{"derivedFrom":[makeQuery(id+"F5.boolean.opBoolean","SPLIT",FACE,{"disambiguationData":[TD([makeQuery(id+"F2.opExtrude","SWEPT_FACE",FACE,{"disambiguationData":[OSD([subQ5])]})])],"derivedFrom":makeQuery(id+"F3.boolean.opBoolean","COPY",FACE,{"derivedFrom":makeQuery(id+"F3.opExtrude","CAP_FACE",FACE,{"disambiguationData":[OSD([subQ5,subQ1,subQ6,subQ7,subQ4,subQ3,subQ2,subQ0])],"isStart":false})})}),makeQuery(id+"F8.opExtrude","SWEPT_FACE",FACE,{"disambiguationData":[OSD([sQuery(id+"F7.wireOp",EDGE,"E67")])]})]});}
            var Q5;
            Q5=makeQuery(id+"F8.boolean.opBoolean","INTERSECT",EDGE,{"disambiguationData":[OD(0.0)],"derivedFrom":[makeQuery(id+"F5.opExtrude","SWEPT_FACE",FACE,{"disambiguationData":[OSD([sQuery(id+"F4.wireOp",EDGE,"E30")])]}),makeQuery(id+"F8.opExtrude","SWEPT_FACE",FACE,{"disambiguationData":[OSD([sQuery(id+"F7.wireOp",EDGE,"E67")])]})]});
            fillet(context, id + "F14", {"entities" : qUnion([Q0, Q1, Q2, Q3, Q4, Q5]), "radius" : 3 * mm, "tangentPropagation" : true, "allowEdgeOverflow" : false});
        }
        {
            var Q0;
            Q0=makeQuery(id+"F1.opExtrude","CAP_EDGE",EDGE,{"disambiguationData":[OSD([sQuery(id+"F0.wireOp",EDGE,"E1.bottom")])],"isStart":false});
            fillet(context, id + "F15", {"entities" : qUnion([Q0]), "radius" : 2 * mm, "tangentPropagation" : true, "allowEdgeOverflow" : false});
        }
        {
            var Q0;
            {var subQ0=sQuery(id+"F0.wireOp",EDGE,"E21.filletArc");var subQ1=sQuery(id+"F0.wireOp",EDGE,"E7");var subQ2=sQuery(id+"F0.wireOp",EDGE,"E6");var subQ3=sQuery(id+"F0.wireOp",EDGE,"E5");var subQ4=sQuery(id+"F0.wireOp",EDGE,"E4");var subQ5=sQuery(id+"F0.wireOp",EDGE,"E22.filletArc");var subQ6=sQuery(id+"F0.wireOp",EDGE,"E1.bottom");var subQ7=sQuery(id+"F0.wireOp",EDGE,"E1.right");var subQ8=sQuery(id+"F0.wireOp",EDGE,"E1.top");var subQ9=sQuery(id+"F0.wireOp",EDGE,"E1.left");var subQ10=sQuery(id+"F0.wireOp",EDGE,"E23.filletArc");var subQ11=sQuery(id+"F0.wireOp",EDGE,"E24.filletArc");Q0=makeQuery(id+"F2.boolean.opBoolean","SPLIT",FACE,{"disambiguationData":[TD([makeQuery(id+"F1.opExtrude","SWEPT_FACE",FACE,{"disambiguationData":[OSD([subQ6])]})])],"derivedFrom":makeQuery(id+"F1.opExtrude","CAP_FACE",FACE,{"disambiguationData":[OSD([subQ6,subQ8,subQ9,subQ7,subQ4,subQ3,subQ2,subQ1,subQ0,subQ5,subQ10,subQ11])],"isStart":true})});}
            var sketch = newSketch(context, id + "F16", { "sketchPlane" : qUnion([Q0])});
            skLineSegment(sketch, "E79", {"start": v(0, 74.25) * mm, "end": v(0, 104.46) * mm, "construction": true});
            skLineSegment(sketch, "E80", {"start": v(-21.48, 74.25) * mm, "end": v(-11.78, 88.6) * mm});
            skLineSegment(sketch, "E81", {"start": v(20.11, 74.25) * mm, "end": v(11.78, 89.43) * mm});
            skLineSegment(sketch, "E82", {"start": v(-11.78, 88.6) * mm, "end": v(-11.78, 104.46) * mm});
            skLineSegment(sketch, "E83", {"start": v(11.78, 89.43) * mm, "end": v(11.78, 104.46) * mm});
            skArc(sketch, "E84", {"start": v(11.78, 104.46) * mm, "mid": v(0, 116.24) * mm, "end": v(-11.78, 104.46) * mm});
            skCircle(sketch, "E85", {"center": v(0, 104.46) * mm, "radius": 5.85 * mm});
            skLineSegment(sketch, "E86", {"start": v(-74.25, 0) * mm, "end": v(74.25, 0) * mm, "construction": true});
            skLineSegment(sketch, "E87.MirrorCS", {"start": v(0, -74.25) * mm, "end": v(0, -104.46) * mm, "construction": true});
            skLineSegment(sketch, "E88.MirrorCS", {"start": v(-21.48, -74.25) * mm, "end": v(-11.78, -88.6) * mm});
            skCircle(sketch, "E89.MirrorC", {"center": v(0, -104.46) * mm, "radius": 5.85 * mm});
            skLineSegment(sketch, "E90.MirrorCS", {"start": v(11.78, -89.43) * mm, "end": v(11.78, -104.46) * mm});
            skArc(sketch, "E91.MirrorCS", {"start": v(11.78, -104.46) * mm, "mid": v(0, -116.24) * mm, "end": v(-11.78, -104.46) * mm});
            skLineSegment(sketch, "E92.MirrorCS", {"start": v(-11.78, -88.6) * mm, "end": v(-11.78, -104.46) * mm});
            skLineSegment(sketch, "E93.MirrorCS", {"start": v(20.11, -74.25) * mm, "end": v(11.78, -89.43) * mm});
            skSolve(sketch);
        }
        {
            var Q0;
            {var subQ0=sQuery(id+"F16.wireOp",EDGE,"E80");Q0=makeQuery(id+"F16.imprint","IMPRINT",FACE,{"disambiguationData":[TD([[makeQuery(id+"F16.imprint","IMPRINT",EDGE,{"derivedFrom":subQ0}),-1.0]])]});}
            var Q1;
            Q1=makeQuery(id+"F16.imprint","IMPRINT",FACE,{"disambiguationData":[TD([[makeQuery(id+"F16.imprint","IMPRINT",EDGE,{"derivedFrom":sQuery(id+"F16.wireOp",EDGE,"E91.MirrorCS")}),-1.0]])]});
            var Q2;
            Q2=makeQuery(id+"F16.imprint","IMPRINT",FACE,{"disambiguationData":[TD([[makeQuery(id+"F16.imprint","IMPRINT",EDGE,{"derivedFrom":makeQuery(id+"F1.opExtrude","CAP_EDGE",EDGE,{"disambiguationData":[OSD([sQuery(id+"F0.wireOp",EDGE,"E1.left")])],"isStart":true})}),-1.0]])]});
            var Q3;
            Q3=makeQuery(id+"F2.opExtrude","CAP_FACE",FACE,{"disambiguationData":[OSD([sQuery(id+"F0.wireOp",EDGE,"E12"),sQuery(id+"F0.wireOp",EDGE,"E13"),sQuery(id+"F0.wireOp",EDGE,"E14"),sQuery(id+"F0.wireOp",EDGE,"E15"),sQuery(id+"F0.wireOp",EDGE,"E17.filletArc"),sQuery(id+"F0.wireOp",EDGE,"E18.filletArc"),sQuery(id+"F0.wireOp",EDGE,"E19.filletArc"),sQuery(id+"F0.wireOp",EDGE,"E20.filletArc"),sQuery(id+"F0.wireOp",EDGE,"E25.0"),sQuery(id+"F0.wireOp",EDGE,"E25.1"),sQuery(id+"F0.wireOp",EDGE,"E25.2"),sQuery(id+"F0.wireOp",EDGE,"E25.3"),sQuery(id+"F0.wireOp",EDGE,"E25.4"),sQuery(id+"F0.wireOp",EDGE,"E25.5"),sQuery(id+"F0.wireOp",EDGE,"E25.6"),sQuery(id+"F0.wireOp",EDGE,"E25.7")])],"isStart":false});
            extrude(context, id + "F17", {"entities" : qUnion([Q0, Q1, Q2]), "endBound" : BoundingType.UP_TO_SURFACE, "endBoundEntityFace" : qUnion([Q3]), "depth" : 25 * mm});
        }
    });
